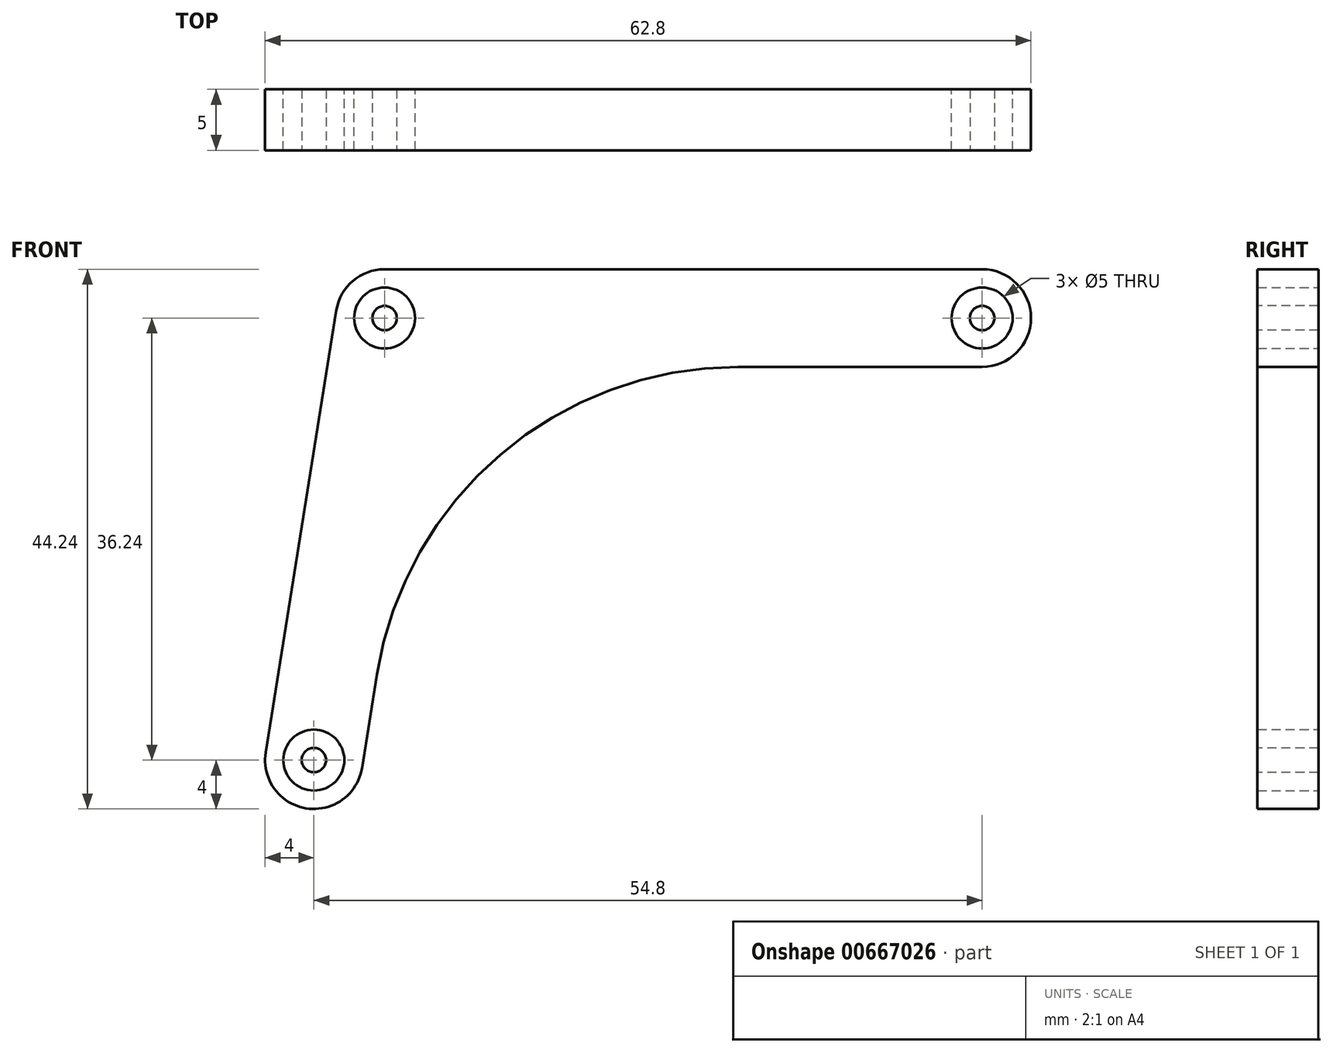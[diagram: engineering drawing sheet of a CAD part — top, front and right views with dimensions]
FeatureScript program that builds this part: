
annotation { "Feature Type Name" : "Feature", "Feature Type Description" : "" }
export const myFeature = defineFeature(function(context is Context, id is Id, definition is map)
    precondition{}
    {
        {
            var Q0;
            Q0=qCreatedBy(makeId("Front.planeOp"),FACE);
            var sketch = newSketch(context, id + "F0", { "sketchPlane" : qUnion([Q0])});
            skArc(sketch, "E0", {"start": v(0, 4) * mm, "mid": v(-2.6, 3.04) * mm, "end": v(-3.95, 0.63) * mm});
            skCircle(sketch, "E1", {"center": v(0, 0) * mm, "radius": 2.5 * mm});
            skArc(sketch, "E2", {"start": v(49, -4) * mm, "mid": v(53, 0) * mm, "end": v(49, 4) * mm});
            skCircle(sketch, "E3", {"center": v(49, 0) * mm, "radius": 2.5 * mm});
            skArc(sketch, "E4", {"start": v(-9.75, -35.6) * mm, "mid": v(-6.43, -40.19) * mm, "end": v(-1.85, -36.87) * mm});
            skCircle(sketch, "E5", {"center": v(-5.8, -36.24) * mm, "radius": 2.5 * mm});
            skLineSegment(sketch, "E6", {"start": v(0, 4) * mm, "end": v(49, 4) * mm});
            skLineSegment(sketch, "E7", {"start": v(3.41, -4) * mm, "end": v(49, -4) * mm});
            skLineSegment(sketch, "E8", {"start": v(-3.95, 0.63) * mm, "end": v(-9.75, -35.6) * mm});
            skLineSegment(sketch, "E9", {"start": v(3.41, -4) * mm, "end": v(-1.85, -36.87) * mm});
            skArc(sketch, "E10", {"start": v(29, -4) * mm, "mid": v(9.53, -11.17) * mm, "end": v(-0.63, -29.26) * mm});
            skSolve(sketch);
        }
        {
            var Q0;
            Q0=makeQuery(id+"F0.imprint","IMPRINT",FACE,{"disambiguationData":[TD([[makeQuery(id+"F0.imprint","IMPRINT",EDGE,{"derivedFrom":sQuery(id+"F0.wireOp",EDGE,"E0")}),1.0]])]});
            var Q1;
            {var subQ3=sQuery(id+"F0.wireOp",EDGE,"E10");Q1=makeQuery(id+"F0.imprint","IMPRINT",FACE,{"disambiguationData":[TD([[makeQuery(id+"F0.imprint","IMPRINT",EDGE,{"derivedFrom":subQ3}),-1.0]])]});}
            extrude(context, id + "F1", {"entities" : qUnion([Q0, Q1]), "endBound" : BoundingType.SYMMETRIC, "depth" : 5 * mm, "offsetDistance" : 25 * mm});
        }
        {
            var Q0;
            Q0=makeQuery(id+"F1.opExtrude","CAP_FACE",FACE,{"disambiguationData":[OSD([sQuery(id+"F0.wireOp",EDGE,"E0"),sQuery(id+"F0.wireOp",EDGE,"E1"),sQuery(id+"F0.wireOp",EDGE,"E2"),sQuery(id+"F0.wireOp",EDGE,"E3"),sQuery(id+"F0.wireOp",EDGE,"E4"),sQuery(id+"F0.wireOp",EDGE,"E5"),sQuery(id+"F0.wireOp",EDGE,"E6"),sQuery(id+"F0.wireOp",EDGE,"E7"),sQuery(id+"F0.wireOp",EDGE,"E8"),sQuery(id+"F0.wireOp",EDGE,"E9"),sQuery(id+"F0.wireOp",EDGE,"E10")])],"isStart":false});
            var sketch = newSketch(context, id + "F2", { "sketchPlane" : qUnion([Q0])});
            skLineSegment(sketch, "E11.0.0", {"start": v(-1.85, -36.87) * mm, "end": v(-0.63, -29.26) * mm});
            skArc(sketch, "E11.0.1", {"start": v(-0.63, -29.26) * mm, "mid": v(9.53, -11.17) * mm, "end": v(29, -4) * mm});
            skLineSegment(sketch, "E11.0.2", {"start": v(29, -4) * mm, "end": v(49, -4) * mm});
            skArc(sketch, "E11.0.3", {"start": v(49, -4) * mm, "mid": v(53, 0) * mm, "end": v(49, 4) * mm});
            skLineSegment(sketch, "E11.0.4", {"start": v(49, 4) * mm, "end": v(0, 4) * mm});
            skArc(sketch, "E11.0.5", {"start": v(0, 4) * mm, "mid": v(-2.6, 3.04) * mm, "end": v(-3.95, 0.63) * mm});
            skLineSegment(sketch, "E11.0.6", {"start": v(-3.95, 0.63) * mm, "end": v(-9.75, -35.6) * mm});
            skArc(sketch, "E11.0.7", {"start": v(-9.75, -35.6) * mm, "mid": v(-6.43, -40.19) * mm, "end": v(-1.85, -36.87) * mm});
            skCircle(sketch, "E12", {"center": v(0, 0) * mm, "radius": 1 * mm});
            skCircle(sketch, "E13", {"center": v(49, 0) * mm, "radius": 1 * mm});
            skCircle(sketch, "E14", {"center": v(-5.8, -36.24) * mm, "radius": 1 * mm});
            skSolve(sketch);
        }
        {
            var Q0;
            Q0=makeQuery(id+"F2.imprint","IMPRINT",FACE,{"disambiguationData":[TD([[makeQuery(id+"F2.imprint","IMPRINT",EDGE,{"derivedFrom":sQuery(id+"F2.wireOp",EDGE,"E12")}),1.0]])]});
            var Q1;
            Q1=makeQuery(id+"F2.imprint","IMPRINT",FACE,{"disambiguationData":[TD([[makeQuery(id+"F2.imprint","IMPRINT",EDGE,{"derivedFrom":sQuery(id+"F2.wireOp",EDGE,"E14")}),1.0]])]});
            var Q2;
            Q2=makeQuery(id+"F2.imprint","IMPRINT",FACE,{"disambiguationData":[TD([[makeQuery(id+"F2.imprint","IMPRINT",EDGE,{"derivedFrom":sQuery(id+"F2.wireOp",EDGE,"E13")}),1.0]])]});
            extrude(context, id + "F3", {"entities" : qUnion([Q0, Q1, Q2]), "oppositeDirection" : true, "depth" : 5 * mm, "offsetDistance" : 25 * mm});
        }
    });
